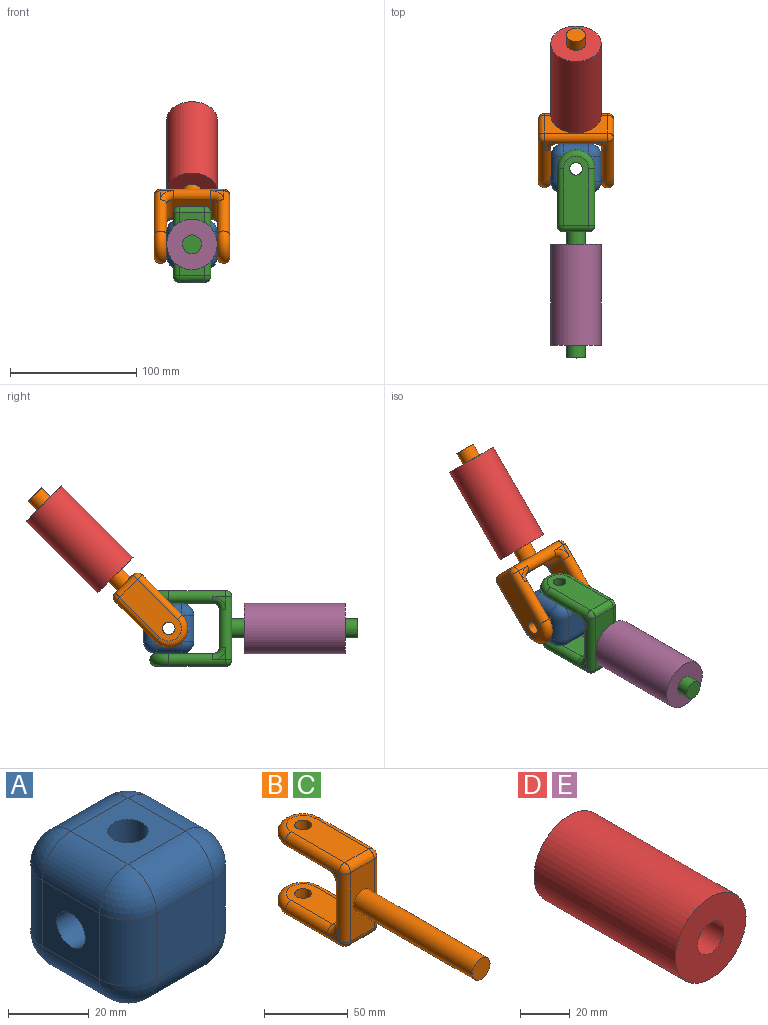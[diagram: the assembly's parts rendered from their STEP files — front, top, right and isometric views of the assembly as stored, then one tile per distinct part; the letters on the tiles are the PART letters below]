
ASSEMBLY  parts=5 mates=4
PART A: 30 faces, bbox 40x40x40 mm
  f0: cylinder r=5mm len=20mm, axis (0,0,-1), area 528.3mm2, adj f6,f8,f9
  f1: plane 20x20mm, normal (-1,0,0), area 321.5mm2, adj f8,f18,f23,f26,f29
  f2: plane 20x20mm, normal (0,-1,0), area 400mm2, adj f15,f24,f25,f29
  f3: plane 20x20mm, normal (1,0,0), area 321.5mm2, adj f9,f10,f14,f15,f16
  f4: plane 20x20mm, normal (0,1,0), area 400mm2, adj f10,f13,f17,f18
  f5: cylinder r=5mm len=20mm, axis (0,0,-1), area 528.3mm2, adj f7,f8,f9
  f6: plane 20x20mm, normal (0,0,1), area 321.5mm2, adj f0,f13,f14,f23,f24
  f7: plane 20x20mm, normal (0,0,-1), area 321.5mm2, adj f5,f16,f17,f25,f26
  f8: cylinder r=5mm len=20mm, axis (1,0,0), area 528.3mm2, adj f0,f1,f5
  f9: cylinder r=5mm len=20mm, axis (1,0,0), area 528.3mm2, adj f0,f3,f5
  f10: cylinder r=10mm len=20mm, axis (0,0,1), area 314.2mm2, adj f3,f4,f11,f12
  f11: sphere r=10mm, area 157.1mm2, adj f10,f13,f14
  f12: sphere r=10mm, area 157.1mm2, adj f10,f16,f17
  f13: cylinder r=10mm len=20mm, axis (1,0,0), area 314.2mm2, adj f4,f6,f11,f19
  f14: cylinder r=10mm len=20mm, axis (0,-1,0), area 314.2mm2, adj f3,f6,f11,f20
  f15: cylinder r=10mm len=20mm, axis (0,0,-1), area 314.2mm2, adj f2,f3,f20,f21
  f16: cylinder r=10mm len=20mm, axis (0,1,0), area 314.2mm2, adj f3,f7,f12,f21
  f17: cylinder r=10mm len=20mm, axis (-1,0,0), area 314.2mm2, adj f4,f7,f12,f22
  f18: cylinder r=10mm len=20mm, axis (0,0,-1), area 314.2mm2, adj f1,f4,f19,f22
  f19: sphere r=10mm, area 157.1mm2, adj f13,f18,f23
  f20: sphere r=10mm, area 157.1mm2, adj f14,f15,f24
  f21: sphere r=10mm, area 157.1mm2, adj f15,f16,f25
  f22: sphere r=10mm, area 157.1mm2, adj f17,f18,f26
  f23: cylinder r=10mm len=20mm, axis (0,1,0), area 314.2mm2, adj f1,f6,f19,f27
  f24: cylinder r=10mm len=20mm, axis (-1,0,0), area 314.2mm2, adj f2,f6,f20,f27
  f25: cylinder r=10mm len=20mm, axis (1,0,0), area 314.2mm2, adj f2,f7,f21,f28
  f26: cylinder r=10mm len=20mm, axis (0,-1,0), area 314.2mm2, adj f1,f7,f22,f28
  f27: sphere r=10mm, area 157.1mm2, adj f23,f24,f29
  f28: sphere r=10mm, area 157.1mm2, adj f25,f26,f29
  f29: cylinder r=10mm len=20mm, axis (0,0,1), area 314.2mm2, adj f1,f2,f27,f28
PART B: 34 faces, bbox 32.5x166.2x60 mm
  f0: plane 10x10mm, normal (1,0,0), area 21.5mm2, adj f20,f21,f24
  f1: plane 10x10mm, normal (1,0,0), area 21.5mm2, adj f14,f16,f20
  f2: plane 10x10mm, normal (-1,0,0), area 21.5mm2, adj f26,f30,f32
  f3: plane 10x10mm, normal (-1,0,0), area 21.5mm2, adj f18,f22,f26
  f4: cylinder r=5mm len=10mm, axis (0,0,-1), area 314.2mm2, adj f5,f6
  f5: plane 55x20mm, normal (0,0,1), area 978.5mm2, adj f4,f14,f15,f18,f23
  f6: plane 45x20mm, normal (0,0,-1), area 778.5mm2, adj f4,f14,f15,f17,f18
  f7: cylinder r=5mm len=10mm, axis (0,0,1), area 314.2mm2, adj f8,f9
  f8: plane 55x20mm, normal (0,0,-1), area 978.5mm2, adj f7,f24,f29,f31,f32
  f9: plane 45x20mm, normal (0,0,1), area 778.5mm2, adj f7,f24,f25,f29,f32
  f10: plane 30x20mm, normal (0,1,0), area 600mm2, adj f17,f20,f25,f26
  f11: plane 50x20mm, normal (0,-1,0), area 823.3mm2, adj f12,f20,f23,f26,f31
  f12: cylinder r=7.5mm len=100mm, axis (0,1,0), area 4712.4mm2, adj f11,f13
  f13: plane 15x15mm, normal (0,-1,0), area 176.7mm2, adj f12
  f14: cylinder r=5mm len=45mm, axis (0,1,0), area 628.3mm2, adj f1,f5,f6,f15,f16,f19
  f15: torus R=10mm, axis (0,0,1), area 650.6mm2, adj f5,f6,f14,f18
  f16: torus R=10mm, axis (1,0,0), area 84.1mm2, adj f1,f14,f17,f20
  f17: cylinder r=5mm len=20mm, axis (1,0,0), area 157.1mm2, adj f6,f10,f16,f22
  f18: cylinder r=5mm len=45mm, axis (0,-1,0), area 628.3mm2, adj f3,f5,f6,f15,f22,f27
  f19: sphere r=5mm, area 39.3mm2, adj f14,f20,f23
  f20: cylinder r=5mm len=50mm, axis (0,0,-1), area 628.3mm2, adj f0,f1,f10,f11,f16,f19,f21,f28
  f21: torus R=10mm, axis (1,0,0), area 84.1mm2, adj f0,f20,f24,f25
  f22: torus R=10mm, axis (1,0,0), area 84.1mm2, adj f3,f17,f18,f26
  f23: cylinder r=5mm len=20mm, axis (-1,0,0), area 157.1mm2, adj f5,f11,f19,f27
  f24: cylinder r=5mm len=45mm, axis (0,1,0), area 628.3mm2, adj f0,f8,f9,f21,f28,f29
  f25: cylinder r=5mm len=20mm, axis (1,0,0), area 157.1mm2, adj f9,f10,f21,f30
  f26: cylinder r=5mm len=50mm, axis (0,0,-1), area 628.3mm2, adj f2,f3,f10,f11,f22,f27,f30,f33
  f27: sphere r=5mm, area 39.3mm2, adj f18,f23,f26
  f28: sphere r=5mm, area 39.3mm2, adj f20,f24,f31
  f29: torus R=10mm, axis (0,0,-1), area 650.6mm2, adj f8,f9,f24,f32
  f30: torus R=10mm, axis (1,0,0), area 84.1mm2, adj f2,f25,f26,f32
  f31: cylinder r=5mm len=20mm, axis (-1,0,0), area 157.1mm2, adj f8,f11,f28,f33
  f32: cylinder r=5mm len=45mm, axis (0,-1,0), area 628.3mm2, adj f2,f8,f9,f29,f30,f33
  f33: sphere r=5mm, area 39.3mm2, adj f26,f31,f32
PART C: same geometry as B
PART D: 4 faces, bbox 40x80x40 mm
  f0: cylinder r=7.5mm len=80mm, axis (0,1,0), area 3769.9mm2, adj f2,f3
  f1: cylinder r=20mm len=80mm, axis (0,1,0), area 10053.1mm2, adj f2,f3
  f2: plane 40x40mm, normal (0,-1,0), area 1079.9mm2, adj f0,f1
  f3: plane 40x40mm, normal (0,1,0), area 1079.9mm2, adj f0,f1
PART E: same geometry as D
PLACE A rot(axis=(0,0,1),179.9deg) t=(0,0,0)mm
PLACE B rot(axis=(-0.68,-0.28,0.68),148.6deg) t=(0,0,0)mm
PLACE C rot(axis=(0,-1,0),0.1deg) t=(0,0,0)mm
PLACE D rot(axis=(1,0,0),45deg) t=(0,70.71,70.71)mm fixed
PLACE E t=(0,-100,0)mm fixed
MATE cylindrical D.f1 <-> B.f12  axis (0,0.71,0.71) through (0,98.99,98.99)mm
MATE revolute C.f4 <-> A.f0  axis (0,0,-1) through (-0.02,0,20)mm
MATE revolute A.f8 <-> B.f4  axis (-1,0,0) through (-20,0.02,-0.02)mm
MATE revolute E.f0 <-> C.f12  axis (0,-1,0) through (0,-140,0)mm
